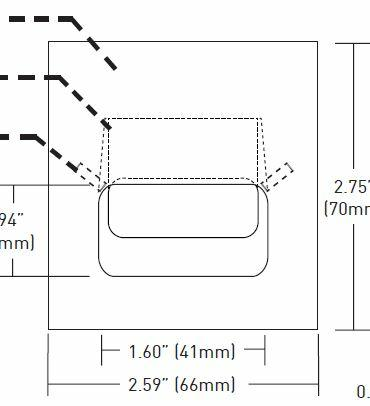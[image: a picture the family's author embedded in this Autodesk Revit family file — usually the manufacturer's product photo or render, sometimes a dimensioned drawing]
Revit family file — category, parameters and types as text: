
# Revit family: Lighting-Steplight-Lucifer-SSL1
name_source: partatom
category: Lighting Fixtures
revit_build: Autodesk Revit 2016 (Build: 20170117_1200(x64)
units: mm (PartAtom-declared; Revit-internal decimal feet)

## family parameters
Cut with Voids When Loaded = No
Host = Face
Light Source = Yes
Part Type = Normal
Room Calculation Point = No
Round Connector Dimension = Use Diameter
Shared = No

## types (1)
- Lighting-Steplight-Lucifer-SSL1
    Apparent Load = 0 VA
    Color Filter = 16777215
    Default Elevation = 4' - 0"
    Description = Steplight
    Dimming Lamp Color Temperature Shift = <None>
    Emit Shape Visible in Rendering = No
    Emit from Rectangle Length = 0' - 1 19/32"
    Emit from Rectangle Width = 0' - 0 15/16"
    Lamp = LED
    Length = 0' - 3"
    Manufacturer = Lucifer Lighting
    Model = SSL1
    Number of Poles = 1
    Photometric Web File = Load File
    Power Factor = 1
    Tilt Angle = -90.00°
    URL = http://www.luciferlighting.com
    Voltage = 0 V
    Width = 0' - 3"

## geometry (parser evidence)
native form markers: Sweep x3
no freeform markers — native parametric forms only
